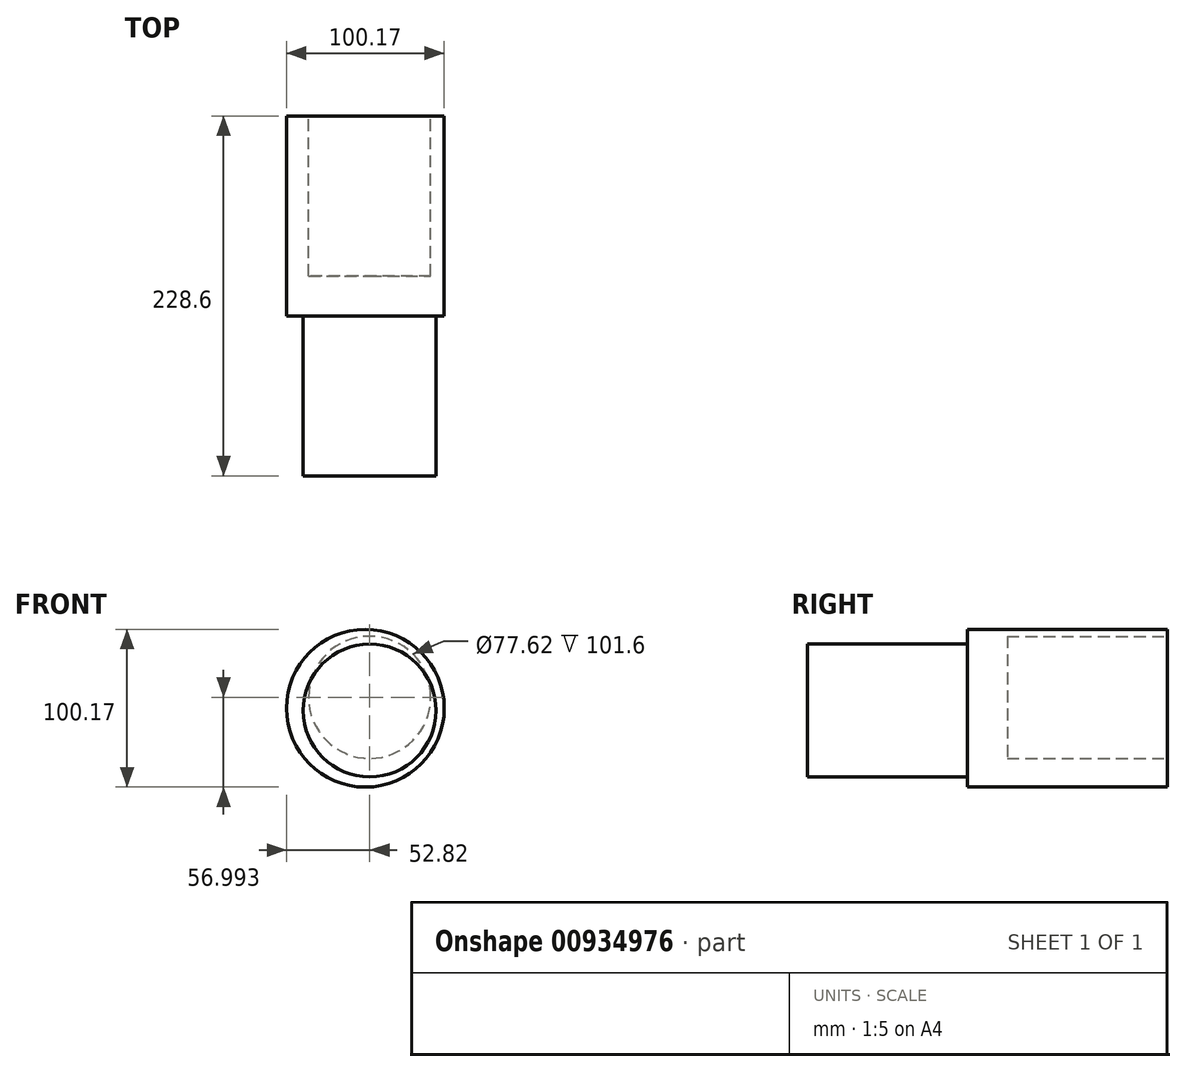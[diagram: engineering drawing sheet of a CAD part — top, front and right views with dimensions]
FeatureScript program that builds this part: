
annotation { "Feature Type Name" : "Feature", "Feature Type Description" : "" }
export const myFeature = defineFeature(function(context is Context, id is Id, definition is map)
    precondition{}
    {
        {
            var Q0;
            Q0=qCreatedBy(makeId("Front.planeOp"),FACE);
            var sketch = newSketch(context, id + "F0", { "sketchPlane" : qUnion([Q0])});
            skCircle(sketch, "E0", {"center": v(-2.73, 9.07) * mm, "radius": 50.09 * mm});
            skSolve(sketch);
        }
        {
            var Q0;
            Q0 = qSketchRegion(id + "F0", true);
            extrude(context, id + "F1", {"entities" : qUnion([Q0]), "depth" : 101.6 * mm, "offsetDistance" : 25.4 * mm});
        }
        {
            var Q0;
            Q0=makeQuery(id+"F1.opExtrude","CAP_FACE",FACE,{"disambiguationData":[OSD([sQuery(id+"F0.wireOp",EDGE,"E0")])],"isStart":false});
            var sketch = newSketch(context, id + "F2", { "sketchPlane" : qUnion([Q0])});
            skCircle(sketch, "E1", {"center": v(0, 7.63) * mm, "radius": 42.18 * mm});
            skSolve(sketch);
        }
        {
            var Q0;
            Q0=makeQuery(id+"F2.imprint","IMPRINT",FACE,{"disambiguationData":[TD([[makeQuery(id+"F2.imprint","IMPRINT",EDGE,{"derivedFrom":sQuery(id+"F2.wireOp",EDGE,"E1")}),1.0]])]});
            extrude(context, id + "F3", {"entities" : qUnion([Q0]), "operationType" : NewBodyOperationType.ADD, "depth" : 101.6 * mm, "offsetDistance" : 25.4 * mm});
        }
        {
            var Q0;
            Q0=makeQuery(id+"F1.opExtrude","CAP_FACE",FACE,{"disambiguationData":[OSD([sQuery(id+"F0.wireOp",EDGE,"E0")])],"isStart":true});
            extrude(context, id + "F4", {"entities" : qUnion([Q0]), "operationType" : NewBodyOperationType.ADD, "depth" : 25.4 * mm, "offsetDistance" : 25.4 * mm});
        }
        {
            var Q0;
            Q0=makeQuery(id+"F4.opExtrude","CAP_FACE",FACE,{"disambiguationData":[OSD([sQuery(id+"F0.wireOp",EDGE,"E0")])],"isStart":false});
            var sketch = newSketch(context, id + "F5", { "sketchPlane" : qUnion([Q0])});
            skCircle(sketch, "E2", {"center": v(0, 15.97) * mm, "radius": 38.8 * mm});
            skSolve(sketch);
        }
        {
            var Q0;
            Q0 = qSketchRegion(id + "F5", true);
            extrude(context, id + "F6", {"entities" : qUnion([Q0]), "operationType" : NewBodyOperationType.REMOVE, "oppositeDirection" : true, "depth" : 101.6 * mm, "offsetDistance" : 25.4 * mm});
        }
    });
